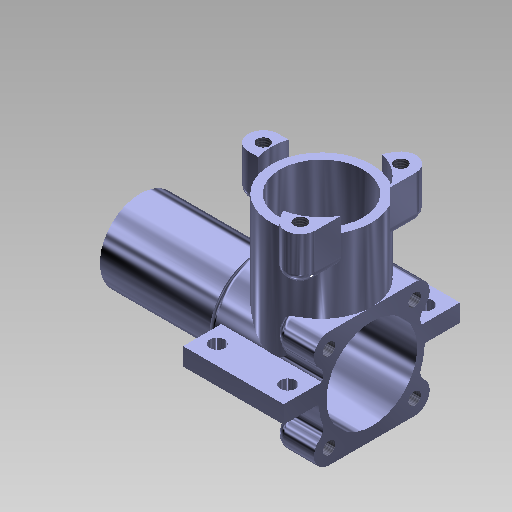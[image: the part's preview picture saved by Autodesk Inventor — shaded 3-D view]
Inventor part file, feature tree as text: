
AUTODESK INVENTOR PART (.ipt)
format: ipt  version: 2018.1 (Build 221171000, 171)  size: 504,832 bytes
history: native  units: in
note: dims shown in document units (in); Inventor stores cm internally (conversion verified against a paired STEP export)
features: sketch x13, extrude x12, thread x7, fillet x3, revolve x1
ambient origin geometry x8: Origin, YZ Plane, XZ Plane, XY Plane, X Axis, Y Axis, Z Axis, Center Point
bodies: Solid1 (feature_tree)
feature tree (36):
  revolve  "Revolution1"  [1 undecoded]
  fillet  "Fillet1"  Radius=1.0236in
  extrude  "Extrusion1"  Depth=0.0787in
  extrude  "Extrusion2"  Depth=0.0787in
  fillet  "Fillet2"  Radius=0.7874in
  extrude  "Extrusion3"  Depth=0.2756in TaperAngle=0.0deg
  fillet  "Fillet3"  Radius=0.6693in
  extrude  "Extrusion4"  Depth=0.3937in TaperAngle=0.0deg
  extrude  "Extrusion5"  Depth=0.3937in TaperAngle=0.0deg
  extrude  "Extrusion6"  Depth=0.3937in TaperAngle=0.0deg
  extrude  "Extrusion7"  Depth=0.3937in TaperAngle=0.0deg
  thread  "Thread5"  [1 undecoded]
  thread  "Thread6"  [1 undecoded]
  thread  "Thread7"  [1 undecoded]
  thread  "Thread8"  [1 undecoded]
  extrude  "Extrusion9"  [1 undecoded]
  thread  "Thread9"  [1 undecoded]
  thread  "Thread10"  [1 undecoded]
  thread  "Thread11"  [1 undecoded]
  extrude  "Extrusion11"  [1 undecoded]
  extrude  "Extrusion13"  [1 undecoded]
  extrude  "Extrusion15"  [1 undecoded]
  extrude  "Extrusion16"  [1 undecoded]
  sketch  "Sketch1"  dims[d4=90.0deg d5=0.0787in d7=1.0236in d8=0.0in]
  sketch  "Sketch2"  dims[d20=0.315in d21=0.0in d22=0.0787in]
  sketch  "Sketch3"  dims[d29=0.1181in d30=0.2362in d31=0.0in d32=0.0in d33=0.0787in d40=0.7874in d41=0.0in]
  sketch  "Sketch4"  dims[d46=0.1969in d47=0.0in d52=0.2756in d53=0.0in d64=0.6693in d65=0.0in]
  sketch  "Sketch7"  dims[d72=0.3937in d73=0.0in d74=0.3937in d75=0.0in]
  sketch  "Sketch8"  dims[d76=0.3937in d77=0.0in d78=0.3937in d79=0.0in]
  sketch  "Sketch9"  dims[d83=0.315in d84=0.0in d85=0.3937in d86=0.0in]
  sketch  "Sketch12"  dims[d87=0.3937in d88=0.0in d89=0.3937in d90=0.0in d94=0.9055in d95=0.0in d100=0.1575in d101=0.0in d106=0.1575in d107=0.0in d109=0.8661in d110=0.0in]
  sketch  "Sketch13"
  sketch  "Sketch14"
  sketch  "Sketch16"
  sketch  "Sketch17"
  sketch  "Sketch18"
note: 13 required parameter values undecoded (feature->parameter linkage not recoverable at this tier; creation-order binding heuristic only, values carry confidence <= 0.55)